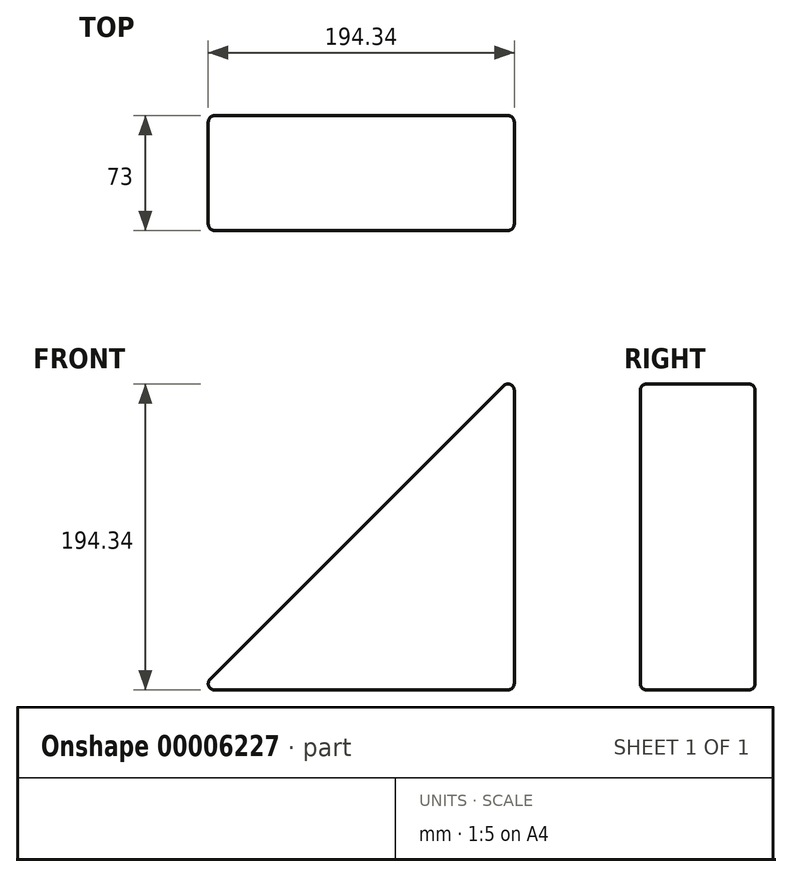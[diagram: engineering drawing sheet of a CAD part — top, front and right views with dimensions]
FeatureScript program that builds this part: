
annotation { "Feature Type Name" : "Feature", "Feature Type Description" : "" }
export const myFeature = defineFeature(function(context is Context, id is Id, definition is map)
    precondition{}
    {
        {
            var Q0;
            Q0=qCreatedBy(makeId("Front.planeOp"),FACE);
            var sketch = newSketch(context, id + "F0", { "sketchPlane" : qUnion([Q0])});
            skLineSegment(sketch, "E0.rect.bottom", {"start": v(100, -100) * mm, "end": v(-100, -100) * mm});
            skLineSegment(sketch, "E0.rect.top", {"start": v(100, 100) * mm, "end": v(-100, 100) * mm, "construction": true});
            skLineSegment(sketch, "E0.rect.left", {"start": v(100, -100) * mm, "end": v(100, 100) * mm});
            skLineSegment(sketch, "E0.rect.right", {"start": v(-100, -100) * mm, "end": v(-100, 100) * mm, "construction": true});
            skPoint(sketch, "E0.rect.middle", {"position": v(0, 0) * mm});
            skLineSegment(sketch, "E1", {"start": v(-100, -100) * mm, "end": v(100, 100) * mm});
            skSolve(sketch);
        }
        {
            var Q0;
            Q0=makeQuery(id+"F0.imprint","IMPRINT",FACE,{"disambiguationData":[TD([[makeQuery(id+"F0.imprint","IMPRINT",EDGE,{"derivedFrom":sQuery(id+"F0.wireOp",EDGE,"E0.rect.bottom")}),-1.0]])]});
            extrude(context, id + "F1", {"entities" : qUnion([Q0]), "depth" : 73 * mm});
        }
        {
            var Q0;
            Q0=makeQuery(id+"F1.opExtrude","CAP_FACE",FACE,{"disambiguationData":[OSD([sQuery(id+"F0.wireOp",EDGE,"E0.rect.bottom"),sQuery(id+"F0.wireOp",EDGE,"E0.rect.left"),sQuery(id+"F0.wireOp",EDGE,"E1")])],"isStart":true});
            var Q1;
            Q1=makeQuery(id+"F1.opExtrude","SWEPT_FACE",FACE,{"disambiguationData":[OSD([sQuery(id+"F0.wireOp",EDGE,"E0.rect.left")])]});
            var Q2;
            Q2=makeQuery(id+"F1.opExtrude","SWEPT_FACE",FACE,{"disambiguationData":[OSD([sQuery(id+"F0.wireOp",EDGE,"E0.rect.bottom")])]});
            var Q3;
            Q3=makeQuery(id+"F1.opExtrude","CAP_FACE",FACE,{"disambiguationData":[OSD([sQuery(id+"F0.wireOp",EDGE,"E0.rect.bottom"),sQuery(id+"F0.wireOp",EDGE,"E0.rect.left"),sQuery(id+"F0.wireOp",EDGE,"E1")])],"isStart":false});
            var Q4;
            Q4=makeQuery(id+"F1.opExtrude","SWEPT_FACE",FACE,{"disambiguationData":[OSD([sQuery(id+"F0.wireOp",EDGE,"E1")])]});
            fillet(context, id + "F2", {"entities" : qUnion([Q0, Q1, Q2, Q3, Q4]), "radius" : 4 * mm, "tangentPropagation" : true, "allowEdgeOverflow" : false});
        }
    });
